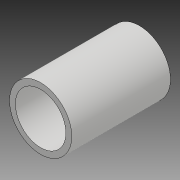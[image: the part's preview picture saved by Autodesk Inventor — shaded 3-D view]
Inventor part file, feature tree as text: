
AUTODESK INVENTOR PART (.ipt)
format: ipt  version: 2018 (Build 220112000, 112)  size: 84,480 bytes
history: native  units: mm
features: extrude x1, sketch x1
ambient origin geometry x8: Origin, YZ Plane, XZ Plane, XY Plane, X Axis, Y Axis, Z Axis, Center Point
bodies: Solid1 (feature_tree)
feature tree (2):
  extrude  "Extrusion1"  Depth=25.4mm
  sketch  "Sketch1"  dims[d0=16.0mm d1=13.0mm d2=25.4mm d3=0.0mm]
